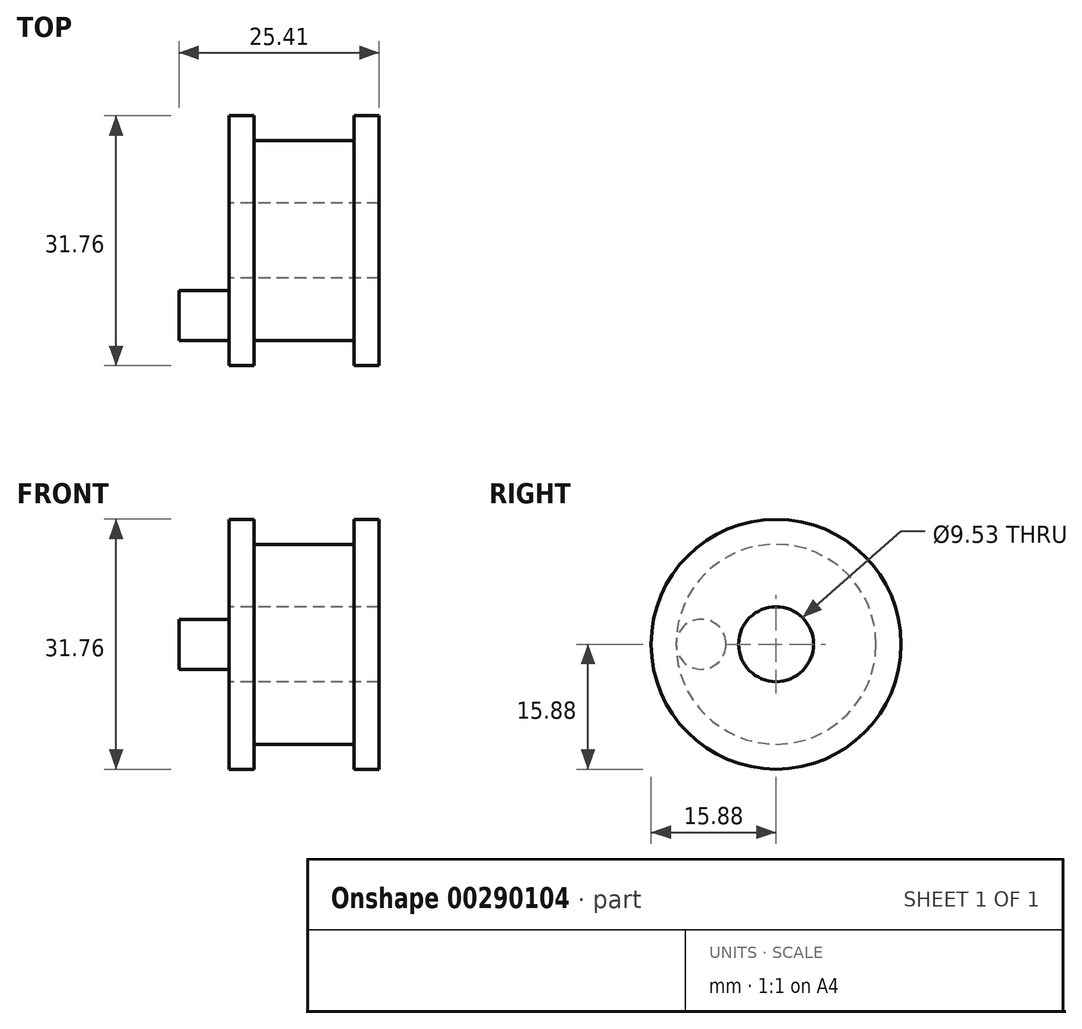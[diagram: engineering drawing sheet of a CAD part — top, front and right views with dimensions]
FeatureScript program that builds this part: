
annotation { "Feature Type Name" : "Feature", "Feature Type Description" : "" }
export const myFeature = defineFeature(function(context is Context, id is Id, definition is map)
    precondition{}
    {
        {
            var Q0;
            Q0=qCreatedBy(makeId("Front.planeOp"),FACE);
            var sketch = newSketch(context, id + "F0", { "sketchPlane" : qUnion([Q0])});
            skLineSegment(sketch, "E0.right", {"start": v(6.35, 12.7) * mm, "end": v(-6.35, 12.7) * mm});
            skPoint(sketch, "E0.middle", {"position": v(0, 0) * mm});
            skLineSegment(sketch, "E1", {"start": v(6.35, 12.7) * mm, "end": v(6.35, 4.76) * mm});
            skLineSegment(sketch, "E2.bottom", {"start": v(-6.35, 15.88) * mm, "end": v(-6.35, 4.76) * mm});
            skLineSegment(sketch, "E2.top", {"start": v(-9.53, 15.88) * mm, "end": v(-9.53, 4.76) * mm});
            skLineSegment(sketch, "E2.left", {"start": v(-6.35, 15.88) * mm, "end": v(-9.53, 15.88) * mm});
            skLineSegment(sketch, "E3.MirrorCS", {"start": v(6.35, 15.88) * mm, "end": v(9.52, 15.88) * mm});
            skLineSegment(sketch, "E4.MirrorCS", {"start": v(6.35, 15.88) * mm, "end": v(6.35, 4.76) * mm});
            skLineSegment(sketch, "E5.MirrorCS", {"start": v(9.52, 15.88) * mm, "end": v(9.52, 4.76) * mm});
            skLineSegment(sketch, "E6", {"start": v(-9.53, 0) * mm, "end": v(9.53, 0) * mm});
            skLineSegment(sketch, "E7", {"start": v(9.52, 4.76) * mm, "end": v(-9.52, 4.76) * mm});
            skSolve(sketch);
        }
        {
            var Q0;
            Q0 = qSketchRegion(id + "F0", true);
            var Q1;
            Q1=sQuery(id+"F0.wireOp",EDGE,"E6");
            revolve(context, id + "F1", {"entities" : qUnion([Q0]), "axis" : qUnion([Q1]), "revolveType" : RevolveType.FULL});
        }
        {
            var Q0;
            Q0=makeQuery(id+"F1.opRevolve","SWEPT_FACE",FACE,{"disambiguationData":[OSD([sQuery(id+"F0.wireOp",EDGE,"E2.top")])]});
            var sketch = newSketch(context, id + "F2", { "sketchPlane" : qUnion([Q0])});
            skCircle(sketch, "E8", {"center": v(9.53, 0) * mm, "radius": 3.18 * mm});
            skSolve(sketch);
        }
        {
            var Q0;
            Q0=makeQuery(id+"F2.imprint","IMPRINT",FACE,{"disambiguationData":[TD([[makeQuery(id+"F2.imprint","IMPRINT",EDGE,{"derivedFrom":sQuery(id+"F2.wireOp",EDGE,"E8")}),1.0]])]});
            extrude(context, id + "F3", {"entities" : qUnion([Q0]), "operationType" : NewBodyOperationType.ADD, "depth" : 6.35 * mm});
        }
    });
